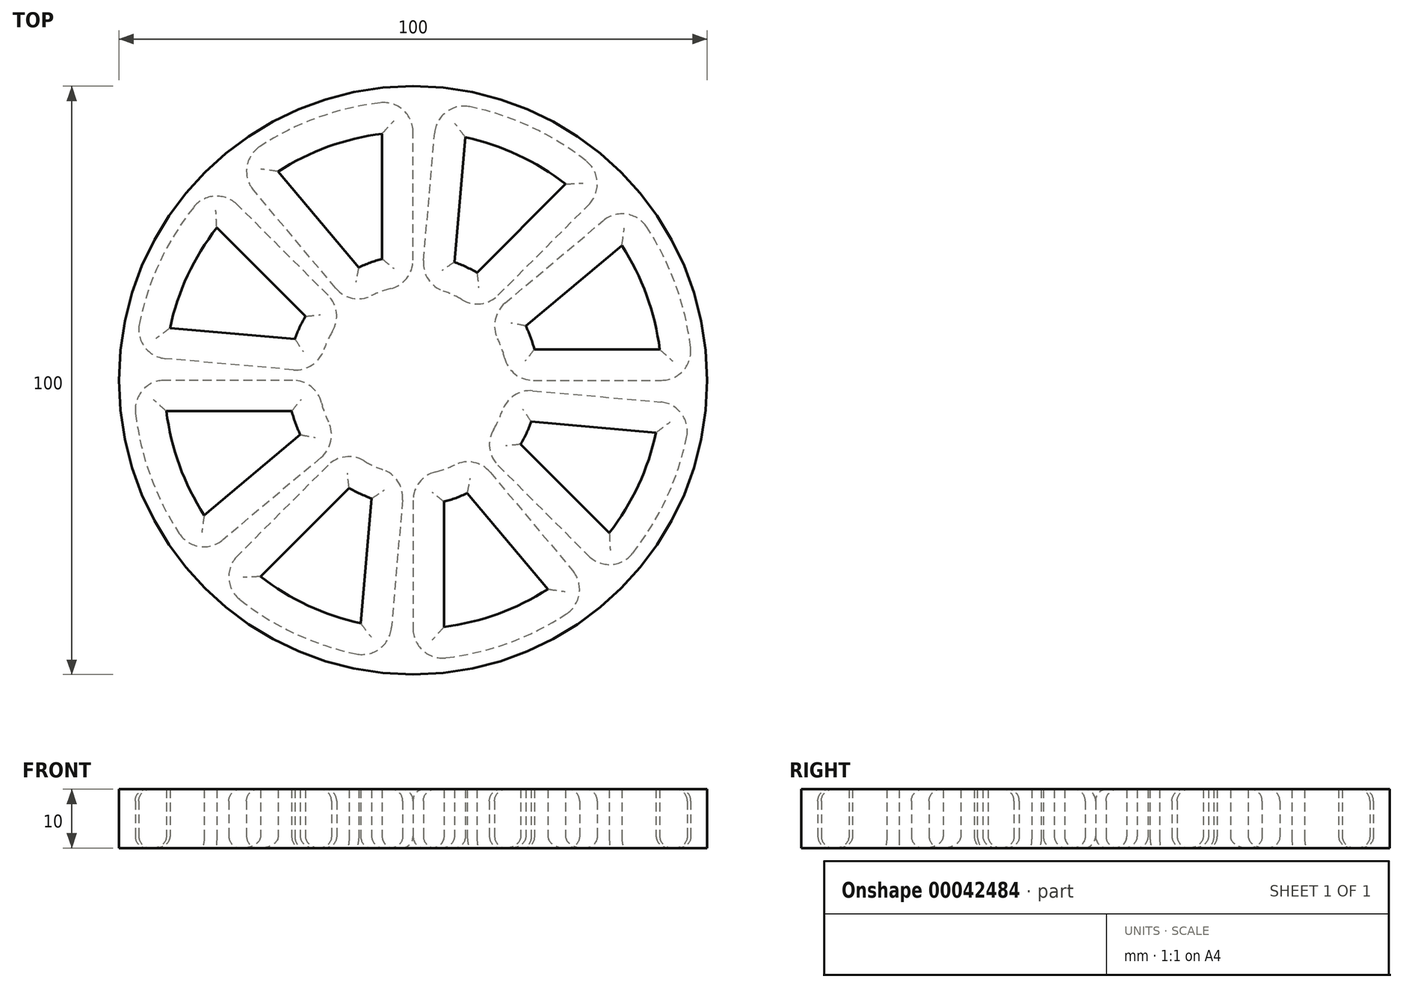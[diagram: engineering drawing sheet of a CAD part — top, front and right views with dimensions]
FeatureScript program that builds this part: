
annotation { "Feature Type Name" : "Feature", "Feature Type Description" : "" }
export const myFeature = defineFeature(function(context is Context, id is Id, definition is map)
    precondition{}
    {
        {
            var Q0;
            Q0=qCreatedBy(makeId("Top.planeOp"),FACE);
            var sketch = newSketch(context, id + "F0", { "sketchPlane" : qUnion([Q0])});
            skLineSegment(sketch, "E0", {"start": v(0, 20.43) * mm, "end": v(0, 42.2) * mm});
            skLineSegment(sketch, "E1", {"start": v(-13.13, 15.65) * mm, "end": v(-27.13, 32.33) * mm});
            skArc(sketch, "E2", {"start": v(-3.81, 15.57) * mm, "mid": v(-5.48, 15.06) * mm, "end": v(-7.09, 14.38) * mm});
            skArc(sketch, "E3", {"start": v(-5.59, 47.17) * mm, "mid": v(-16.25, 44.64) * mm, "end": v(-26.04, 39.73) * mm});
            skPoint(sketch, "E4.visualSharp", {"position": v(-30.53, 36.39) * mm});
            skArc(sketch, "E4.filletArc", {"start": v(-26.04, 39.73) * mm, "mid": v(-28.25, 36.27) * mm, "end": v(-27.13, 32.33) * mm});
            skPoint(sketch, "E5.visualSharp", {"position": v(0, 47.5) * mm});
            skArc(sketch, "E5.filletArc", {"start": v(0, 42.2) * mm, "mid": v(-1.68, 45.94) * mm, "end": v(-5.59, 47.17) * mm});
            skPoint(sketch, "E6.visualSharp", {"position": v(0, 16.03) * mm});
            skArc(sketch, "E6.filletArc", {"start": v(-3.81, 15.57) * mm, "mid": v(-1.07, 17.34) * mm, "end": v(0, 20.43) * mm});
            skPoint(sketch, "E7.visualSharp", {"position": v(-10.3, 12.28) * mm});
            skArc(sketch, "E7.filletArc", {"start": v(-13.13, 15.65) * mm, "mid": v(-10.33, 13.97) * mm, "end": v(-7.09, 14.38) * mm});
            skArc(sketch, "E8.0", {"start": v(-5.25, 41.92) * mm, "mid": v(-14.45, 39.7) * mm, "end": v(-22.92, 35.49) * mm});
            skLineSegment(sketch, "E8.1", {"start": v(-5.25, 20.62) * mm, "end": v(-5.25, 41.92) * mm});
            skArc(sketch, "E8.2", {"start": v(-5.25, 20.62) * mm, "mid": v(-7.28, 20) * mm, "end": v(-9.23, 19.17) * mm});
            skLineSegment(sketch, "E8.3", {"start": v(-9.23, 19.17) * mm, "end": v(-22.92, 35.49) * mm});
            skSolve(sketch);
        }
        {
            var Q0;
            Q0 = qSketchRegion(id + "F0", true);
            extrude(context, id + "F1", {"entities" : qUnion([Q0]), "depth" : 10 * mm});
        }
        {
            var Q0;
            Q0=makeQuery(id+"F1.opExtrude","CAP_EDGE",EDGE,{"disambiguationData":[OSD([sQuery(id+"F0.wireOp",EDGE,"E1")])],"isStart":false});
            fillet(context, id + "F2", {"entities" : qUnion([Q0]), "radius" : 2 * mm, "tangentPropagation" : true, "allowEdgeOverflow" : false});
        }
        {
            var Q0;
            Q0=makeQuery(id+"F1.opExtrude","CAP_EDGE",EDGE,{"disambiguationData":[OSD([sQuery(id+"F0.wireOp",EDGE,"E8.3")])],"isStart":true});
            var Q1;
            Q1=makeQuery(id+"F1.opExtrude","CAP_EDGE",EDGE,{"disambiguationData":[OSD([sQuery(id+"F0.wireOp",EDGE,"E8.0")])],"isStart":true});
            var Q2;
            Q2=makeQuery(id+"F1.opExtrude","CAP_EDGE",EDGE,{"disambiguationData":[OSD([sQuery(id+"F0.wireOp",EDGE,"E8.1")])],"isStart":true});
            var Q3;
            Q3=makeQuery(id+"F1.opExtrude","CAP_EDGE",EDGE,{"disambiguationData":[OSD([sQuery(id+"F0.wireOp",EDGE,"E8.2")])],"isStart":true});
            var Q4;
            Q4=makeQuery(id+"F1.opExtrude","CAP_EDGE",EDGE,{"disambiguationData":[OSD([sQuery(id+"F0.wireOp",EDGE,"E1")])],"isStart":true});
            fillet(context, id + "F3", {"entities" : qUnion([Q0, Q1, Q2, Q3, Q4]), "radius" : 2 * mm, "tangentPropagation" : true, "allowEdgeOverflow" : false});
        }
        {
            var Q0;
            Q0=qCreatedBy(makeId("Front.planeOp"),FACE);
            var sketch = newSketch(context, id + "F4", { "sketchPlane" : qUnion([Q0])});
            skLineSegment(sketch, "E9", {"start": v(0, 50.96) * mm, "end": v(0, -51.6) * mm, "construction": true});
            skSolve(sketch);
        }
        {
            var Q0;
            Q0=makeQuery(id+"F1.opExtrude","SWEPT_BODY",BODY,{"disambiguationData":[OSD([sQuery(id+"F0.wireOp",EDGE,"E0"),sQuery(id+"F0.wireOp",EDGE,"E1"),sQuery(id+"F0.wireOp",EDGE,"E2"),sQuery(id+"F0.wireOp",EDGE,"E3"),sQuery(id+"F0.wireOp",EDGE,"E4.filletArc"),sQuery(id+"F0.wireOp",EDGE,"E5.filletArc"),sQuery(id+"F0.wireOp",EDGE,"E6.filletArc"),sQuery(id+"F0.wireOp",EDGE,"E7.filletArc"),sQuery(id+"F0.wireOp",EDGE,"E8.0"),sQuery(id+"F0.wireOp",EDGE,"E8.1"),sQuery(id+"F0.wireOp",EDGE,"E8.2"),sQuery(id+"F0.wireOp",EDGE,"E8.3")])]});
            var Q1;
            Q1=sQuery(id+"F4.wireOp",EDGE,"E9");
            circularPattern(context, id + "F5", {"entities" : qUnion([Q0]), "axis" : qUnion([Q1]), "angle" : 45 * degree, "instanceCount" : 8});
        }
        {
            var Q0;
            Q0=qCreatedBy(makeId("Top.planeOp"),FACE);
            var sketch = newSketch(context, id + "F6", { "sketchPlane" : qUnion([Q0])});
            skCircle(sketch, "E10", {"center": v(0, 0) * mm, "radius": 50 * mm});
            skSolve(sketch);
        }
        {
            var Q0;
            Q0 = qSketchRegion(id + "F6", true);
            extrude(context, id + "F7", {"entities" : qUnion([Q0]), "depth" : 10 * mm});
        }
    });
